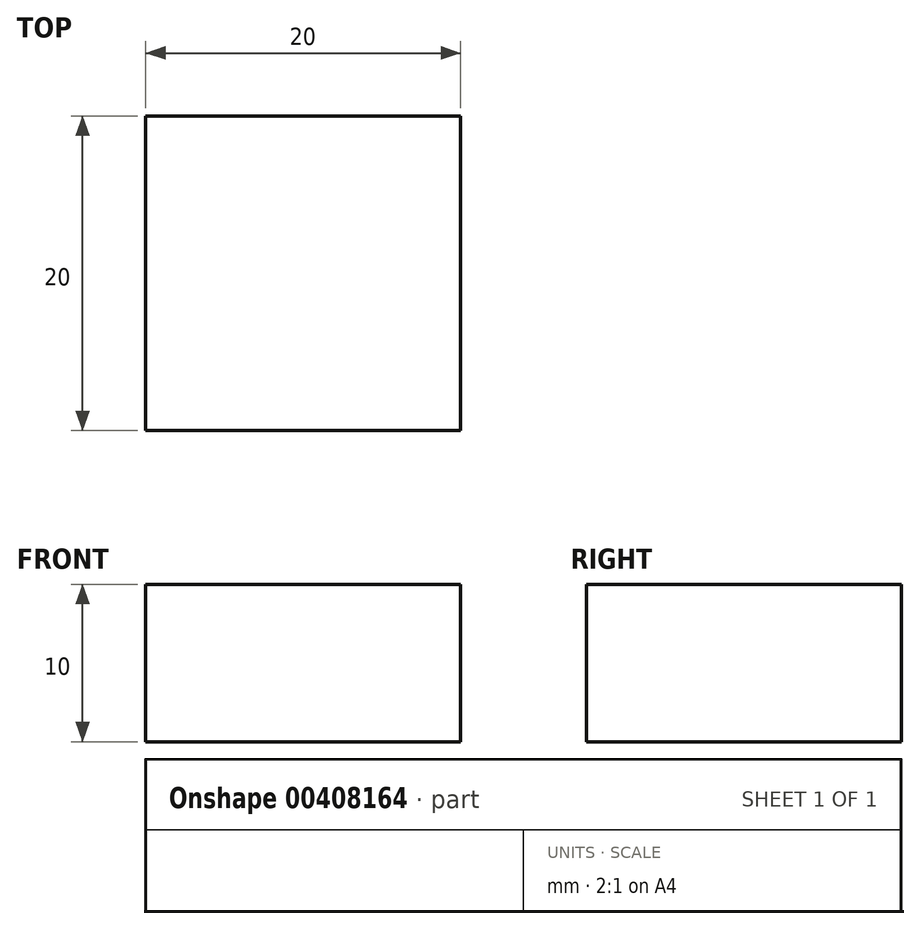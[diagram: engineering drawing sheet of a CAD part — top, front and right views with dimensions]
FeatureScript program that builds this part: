
annotation { "Feature Type Name" : "Feature", "Feature Type Description" : "" }
export const myFeature = defineFeature(function(context is Context, id is Id, definition is map)
    precondition{}
    {
        {
            var Q0;
            Q0=qCreatedBy(makeId("Top.planeOp"),FACE);
            var sketch = newSketch(context, id + "F0", { "sketchPlane" : qUnion([Q0])});
            skLineSegment(sketch, "E0.bottom", {"start": v(10, 10) * mm, "end": v(-10, 10) * mm});
            skLineSegment(sketch, "E0.top", {"start": v(10, -10) * mm, "end": v(-10, -10) * mm});
            skLineSegment(sketch, "E0.left", {"start": v(10, 10) * mm, "end": v(10, -10) * mm});
            skLineSegment(sketch, "E0.right", {"start": v(-10, 10) * mm, "end": v(-10, -10) * mm});
            skPoint(sketch, "E0.middle", {"position": v(0, 0) * mm});
            skSolve(sketch);
        }
        {
            var Q0;
            Q0 = qSketchRegion(id + "F0", true);
            extrude(context, id + "F1", {"entities" : qUnion([Q0]), "depth" : 10 * mm});
        }
    });
